# Revit family: Electronics_Huddle-Room-Solutions_Biamp_Devio_Conferencing-Hub_SCR-10__
name_source: partatom
category: Communication Devices
units: mm (PartAtom-declared; Revit-internal decimal feet)

## family parameters
Cut with Voids When Loaded = No
Host = Face
Maintain Annotation Orientation = No
OmniClass Number = 23.85.10.17.11.11
OmniClass Title = Broadcasting Receiving Equipment
Part Type = Normal
Room Calculation Point = No
Round Connector Dimension = Use Diameter
Shared = No

## types (1)
- SCR-10
    Apparent Load = 15 VA
    Compliance = CE Marked (Europe) RoHS Directive (Europe)
    Connector Description = 5V DC 15W
    Default Elevation = 4' - 0"
    Depth = 0' - 3 11/32"
    Description = Devio® SCR-10 Conferencing Hub
    HDCP Support = 2.0
    Height = 0' - 0 29/32"
    Housing Material = Biamp - Plastic - White
    Humidity = 10-90% relative humidity (non-condensing)
    Included Accessories = 3m USB 3.0 cable Mounting screws Zip ties
    Manufacturer = Biamp
    Max Power Consumption = 15 W
    Model = Devio SCR-10
    Network Connection = RJ-45 with Ethernet cable (Cat 5e and above)
    Number of Poles = 1
    Physical Interfaces = HDMI
    Power Factor = 1
    Product Documentation Link = https://downloads.biamp.com
    Product Page URL = https://www.biamp.com
    Product data url = https://www.bimobject.com
    Status Indicator = Status Indicator (Green/Red LED)
    Supported Resolutions = Up to 4096 x 2160p (60fps)
    Temperature Range = 50-86° F (10-30° C)
    URL = https://www.biamp.com
    Voltage = 5 V
    Weight = 0.40 lbf
    Width = 0' - 7 11/32"

## geometry (parser evidence)
native form markers: Sweep x1
no freeform markers — native parametric forms only
